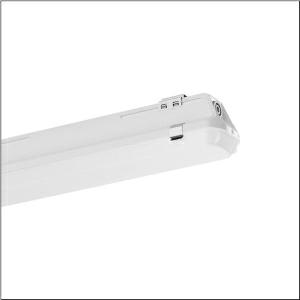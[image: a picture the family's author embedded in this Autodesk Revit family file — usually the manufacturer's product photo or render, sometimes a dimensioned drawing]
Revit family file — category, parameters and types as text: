
# Revit family: monsun_r__21_51fb107p480b005_c053
name_source: partatom
category: Lighting Fixtures
units: mm (PartAtom-declared; Revit-internal decimal feet)

## family parameters
Cut with Voids When Loaded = No
Host = Face
Light Source = No
Part Type = Normal
Room Calculation Point = No
Round Connector Dimension = Use Diameter
Shared = No

## types (1)
- Monsun® 21 (1 x LED, 8070 lm, 52.8 W, 4000K)
    Apparent Load = 53 VA
    CIE Flux Codes = 47 77 93 94 100
    Color Rendering = 80
    Color Temperature = 4000K
    Default Elevation = 1800 mm
    Description = Monsun® 21, damp-proof luminaire, chain hanger, primary optical cover: enclosure, of PMMA, light emission: direct distribution, primary light characteristic: symmetric, installation type: suspended mounting, surface-mounted, horizontal mounting, vertical mounting, LED, rated luminous flux: 8.070lm, luminous efficacy: 153lm/W, light colour: 840, colour temperature: 4000K, control gear: ECG, with terminal, 3-pole, max. 2.5mm², through-wiring: 5x 2.5mm², mains connection: 220..240V, AC, 50/60Hz, rated input power: 53W, housing, of glass-fibre reinforced polyester, uncoated, bright grey, incl. chain hanger, length: 1.590mm, width: 90mm, height: 88mm, clip for enclosure, of stainless steel (V2A), ceiling mounting element, of stainless steel (V2A), chain hanger, of stainless steel (V2A), protection rating (complete): IP66, insulation class (complete): insulation class I (protective earthing), certification: CE, ENEC, VDE, UKCA, protection symbol: D, impact resistance: IK04, permissible operating ambient temperature: -25..+35°C, standard: EN 50419, EN 60598-2-1, corresponds to IFS (International Featured Standards) requirements for safety and quality in the food industry, for indoor or canopied outdoor use, no direct snow, no direct sun, no direct rain, contact your sales advisor before using the luminaires in applications with unclear chemical exposure, large temperature fluctuations or condensation-forming humidity, LABS conformity tested according to VDMA 24364:2018-05, packaging unit: 1 piece
    Height = 89 mm
    Lamp = 1 x LED
    Lamp Light Flux = 8070 lm
    Lamp Power = 52.8 W
    Lamp count = 1
    Length = 1590 mm
    Luminous efficacy = 153 lm/W
    Manufacturer = Siteco
    ModVariant = No
    Model = 51FB107P480B005
    Mounting Place = Ceiling
    Mounting Type = Surface mounted
    Number of Poles = 1
    OnlyDefault = Yes
    Power Factor = 1
    Product Name = Monsun® 21
    Product group = damp-proof luminaire
    ProductGroupID = 301
    Protection Class = Protection class I
    Protection Degree = IP 66
    RLX_Detail_Level = 1
    RLX_Emergency_Light_Flux = 0 lm
    RLX_Emergency_Type = 0
    RLX_Emergency_Type_DB = No
    RlxData = <blob elided: 88337 chars, md5=cbc9f799>
    Socket = socket
    Standby Power = 0 W
    System Light Flux = 8070 lm
    System Power = 53 W
    Type Comments = Product without accessories
    Type Image = l_1006717.jpg
    URL = http://relux.com
    VarID = ---
    Voltage = 0 V
    Weight = 0.00 kg
    Width = 90 mm

## geometry (parser evidence)
native form markers: Blend x4, Sweep x11
no freeform markers — native parametric forms only
